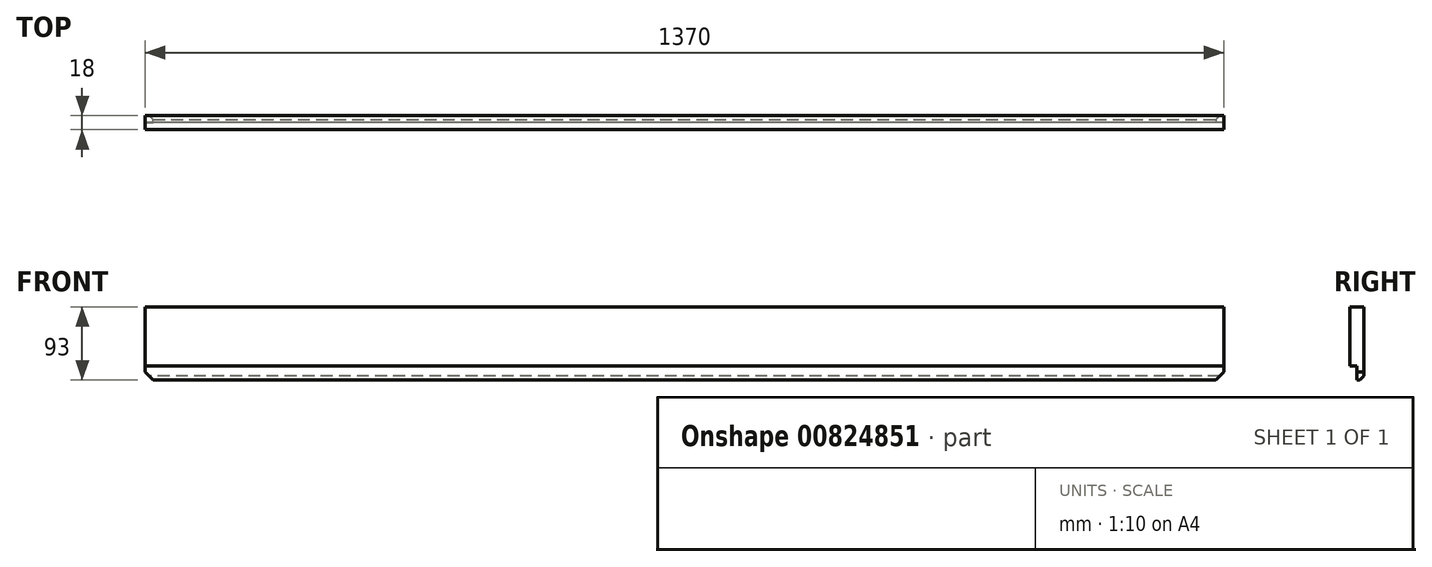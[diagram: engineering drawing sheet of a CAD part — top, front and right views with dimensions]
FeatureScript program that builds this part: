
annotation { "Feature Type Name" : "Feature", "Feature Type Description" : "" }
export const myFeature = defineFeature(function(context is Context, id is Id, definition is map)
    precondition{}
    {
        {
            var Q0;
            Q0=qCreatedBy(makeId("Front.planeOp"),FACE);
            var sketch = newSketch(context, id + "F0", { "sketchPlane" : qUnion([Q0])});
            skLineSegment(sketch, "E0.bottom", {"start": v(685, 46.5) * mm, "end": v(-685, 46.5) * mm});
            skLineSegment(sketch, "E0.top", {"start": v(685, -46.5) * mm, "end": v(-685, -46.5) * mm});
            skLineSegment(sketch, "E0.left", {"start": v(685, 46.5) * mm, "end": v(685, -46.5) * mm});
            skLineSegment(sketch, "E0.right", {"start": v(-685, 46.5) * mm, "end": v(-685, -46.5) * mm});
            skPoint(sketch, "E0.middle", {"position": v(0, 0) * mm});
            skSolve(sketch);
        }
        {
            var Q0;
            Q0 = qSketchRegion(id + "F0", true);
            extrude(context, id + "F1", {"entities" : qUnion([Q0]), "depth" : 9 * mm, "offsetDistance" : 25 * mm});
        }
        {
            var Q0;
            Q0=makeQuery(id+"F1.opExtrude","CAP_FACE",FACE,{"disambiguationData":[OSD([sQuery(id+"F0.wireOp",EDGE,"E0.bottom"),sQuery(id+"F0.wireOp",EDGE,"E0.top"),sQuery(id+"F0.wireOp",EDGE,"E0.left"),sQuery(id+"F0.wireOp",EDGE,"E0.right")])],"isStart":false});
            var sketch = newSketch(context, id + "F2", { "sketchPlane" : qUnion([Q0])});
            skLineSegment(sketch, "E1.bottom", {"start": v(685, 46.5) * mm, "end": v(-685, 46.5) * mm});
            skLineSegment(sketch, "E1.top", {"start": v(685, -28.5) * mm, "end": v(-685, -28.5) * mm});
            skLineSegment(sketch, "E1.left", {"start": v(685, 46.5) * mm, "end": v(685, -28.5) * mm});
            skLineSegment(sketch, "E1.right", {"start": v(-685, 46.5) * mm, "end": v(-685, -28.5) * mm});
            skSolve(sketch);
        }
        {
            var Q0;
            Q0 = qSketchRegion(id + "F2", true);
            extrude(context, id + "F3", {"entities" : qUnion([Q0]), "operationType" : NewBodyOperationType.ADD, "depth" : 9 * mm, "offsetDistance" : 25 * mm});
        }
        {
            var Q0;
            Q0=makeQuery(id+"F1.opExtrude","SWEPT_EDGE",EDGE,{"disambiguationData":[OSD([sQuery(id+"F0.wireOp",EDGE,"E0.top"),sQuery(id+"F0.wireOp",EDGE,"E0.left")])]});
            var Q1;
            Q1=makeQuery(id+"F1.opExtrude","SWEPT_EDGE",EDGE,{"disambiguationData":[OSD([sQuery(id+"F0.wireOp",EDGE,"E0.top"),sQuery(id+"F0.wireOp",EDGE,"E0.right")])]});
            chamfer(context, id + "F4", {"entities" : qUnion([Q0, Q1]), "width" : 10 * mm, "tangentPropagation" : true});
        }
        {
            var Q0;
            Q0=makeQuery(id+"F1.opExtrude","CAP_EDGE",EDGE,{"disambiguationData":[OSD([sQuery(id+"F0.wireOp",EDGE,"E0.top")])],"isStart":true});
            chamfer(context, id + "F5", {"entities" : qUnion([Q0]), "width" : 5 * mm, "tangentPropagation" : true});
        }
    });
